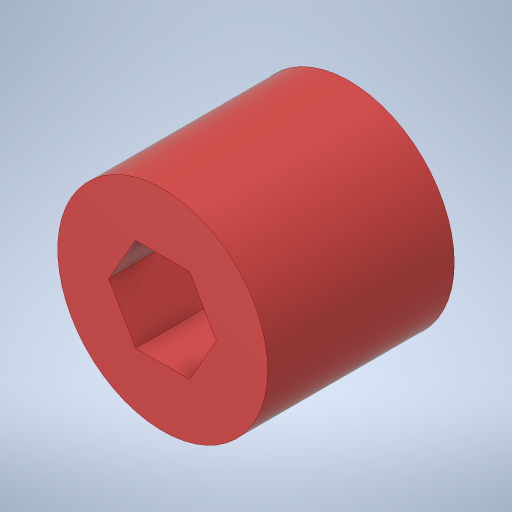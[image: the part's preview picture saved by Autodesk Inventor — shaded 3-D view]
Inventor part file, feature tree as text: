
AUTODESK INVENTOR PART (.ipt)
format: ipt  version: 2023.3 (Build 273359000, 359)  size: 221,184 bytes
history: native  units: in
note: dims shown in document units (in); Inventor stores cm internally (conversion verified against a paired STEP export)
features: extrude x1, sketch x1
ambient origin geometry x8: Origin, YZ Plane, XZ Plane, XY Plane, X Axis, Y Axis, Z Axis, Center Point
bodies: Solid1 (feature_tree)
feature tree (2):
  extrude  "Extrusion1"  Depth=0.5in
  sketch  "Sketch1"  dims[d0=1.125in d1=0.5in d2=1.0in d3=0.0in]
